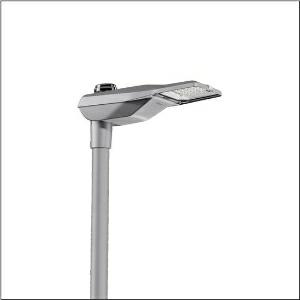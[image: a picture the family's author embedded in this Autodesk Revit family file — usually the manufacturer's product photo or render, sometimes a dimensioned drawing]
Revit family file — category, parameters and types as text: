
# Revit family: streetlight_sl_21_micro___st1_0a_5xe5d37n08db_4323
name_source: partatom
category: Lighting Fixtures
units: mm (PartAtom-declared; Revit-internal decimal feet)

## family parameters
Cut with Voids When Loaded = No
Host = Face
Light Source = No
Part Type = Normal
Room Calculation Point = No
Round Connector Dimension = Use Diameter
Shared = No

## types (1)
- --- (1 x LED, 5110 lm, 39.1 W, 3000K)
    Apparent Load = 39 VA
    CIE Flux Codes = 37 72 97 100 100
    Color Rendering = 70
    Color Temperature = 3000K
    Default Elevation = 1800 mm
    Description = Streetlight SL 21 micro, mast luminaire, primary light control with lens, of PMMA, primary optical cover: cover, of toughened safety glass, transparent, light distribution: ST1.0a, light emission: direct distribution, primary light characteristic: asymmetric, installation type: post-top, LED, 3G 1.5mm², High Power LED, rated luminous flux: 5.110lm, luminous efficacy: 131lm/W, light colour: 730, colour temperature: 3000K, control gear: NEMA (7pin), control: overheat protection, pre-setting: linear dimming characteristic, constant luminous flux control, time-dependent luminous flux control, flexible luminous flux parameterisation, mains connection: 230..240V, AC, 50/60Hz, connection cable pre-assembled, cable length: 6,5m, wiring characteristics: H07RN-F, start of lifetime: 39W, end of service life: 41W, reduction: 18W, luminaire housing, of diecast aluminium (EN AC-44300), powder-coated, SITECO metallic grey (DB 702S), corrosivity category C5 high according to DIN EN ISO 12944, multi-level sealing system, sealing non-destructively replaceable, inclination adjustable: 0°, 5°, 10°, 15°, length: 528mm, width: 235mm, height: 110mm, spigot size: 76/60mm (post-top), mounting height: 4..8m, protection rating (complete): IP66, insulation class (complete): insulation class I (protective earthing), certification: CE, ENEC, ENEC+, VDE, impact resistance: IK10, permissible operating ambient temperature for outdoor applications: -40..+50°C, standard-compliant lighting for roads and squares, packaging unit: 1 piece

Light Distribution: ST1.0a
    Height = 110 mm
    Lamp = 1 x LED
    Lamp Light Flux = 5110 lm
    Lamp Power = 39.1 W
    Lamp count = 1
    Length = 528 mm
    Luminous efficacy = 131 lm/W
    Manufacturer = Siteco
    ModVariant = No
    Model = 5XE5D37N08DB
    Number of Poles = 1
    OnlyDefault = Yes
    Power Factor = 1
    Product Name = Streetlight SL 21 micro | ST1.0a
    Product group = mast luminaire | pylon top
    ProductGroupID = 6100
    Protection Class = Protection class I
    Protection Degree = IP 66
    RLX_Detail_Level = 1
    RLX_Emergency_Light_Flux = 0 lm
    RLX_Emergency_Type = 0
    RLX_Emergency_Type_DB = No
    RlxData = <blob elided: 99021 chars, md5=78cd45b8>
    Socket = socket
    Standby Power = 0 W
    System Light Flux = 5110 lm
    System Power = 39 W
    Type Comments = factory setting: luminous flux: 100 % | dim-lin: 254 | 765 mA
    Type Image = l_1294375.jpg
    URL = http://relux.com
    VarID = @adj_136041
    Voltage = 0 V
    Weight = 0.00 kg
    Width = 235 mm

## geometry (parser evidence)
native form markers: Blend x4, Sweep x10
no freeform markers — native parametric forms only
